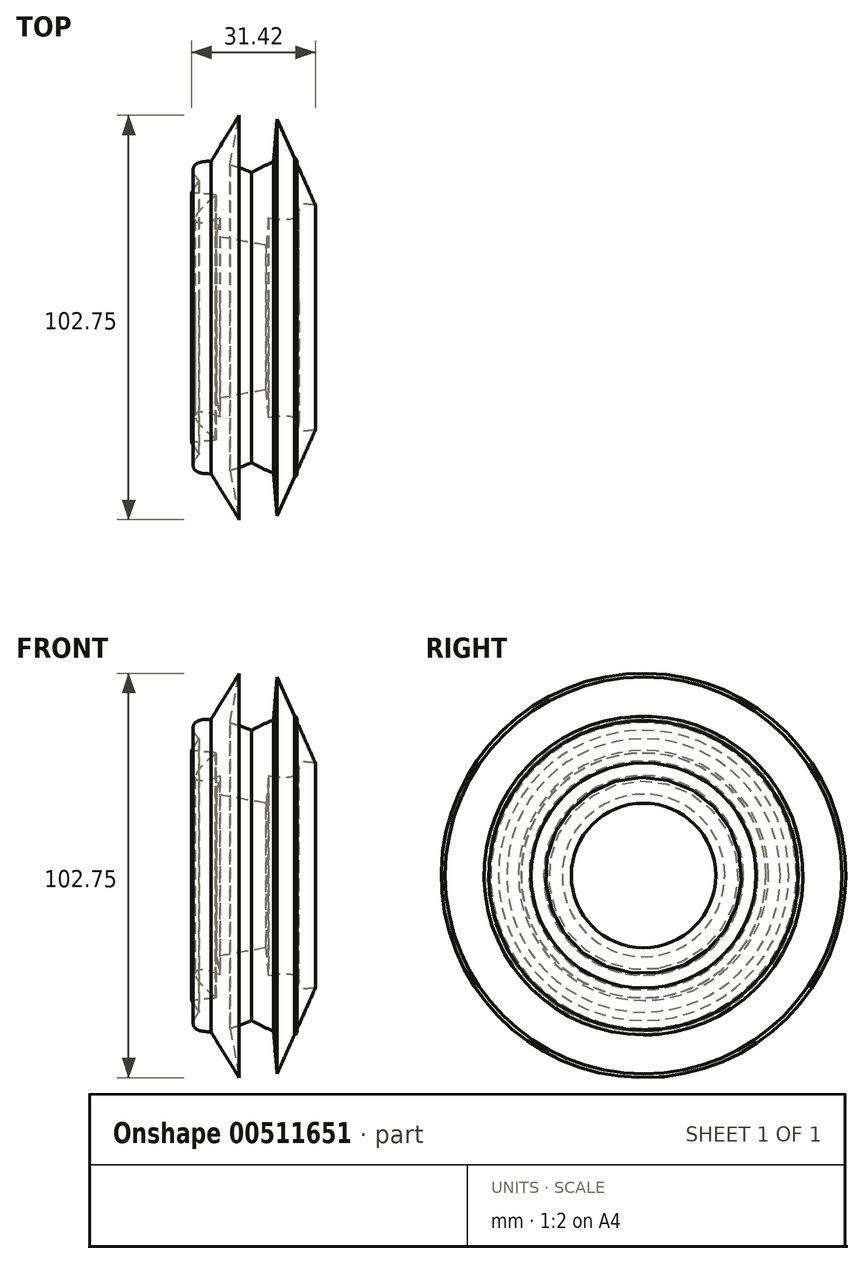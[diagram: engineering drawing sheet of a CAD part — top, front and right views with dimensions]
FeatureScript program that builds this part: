
annotation { "Feature Type Name" : "Feature", "Feature Type Description" : "" }
export const myFeature = defineFeature(function(context is Context, id is Id, definition is map)
    precondition{}
    {
        {
            var Q0;
            Q0=qCreatedBy(makeId("Front.planeOp"),FACE);
            var sketch = newSketch(context, id + "F0", { "sketchPlane" : qUnion([Q0])});
            skEllipse(sketch, "E0", {"center": v(0, -41.42) * mm, "majorRadius": 14.6 * mm, "minorRadius": 4.76 * mm, "majorAxis": v(0.9, 0.41)});
            skEllipse(sketch, "E1", {"center": v(0, -41.42) * mm, "majorRadius": 15.03 * mm, "minorRadius": 3.32 * mm, "majorAxis": v(-0.85, 0.52)});
            skLineSegment(sketch, "E2", {"start": v(-13.82, -40.88) * mm, "end": v(-1.74, -60.59) * mm});
            skPoint(sketch, "E2.endSnap0", {"position": v(-1.74, -44.24) * mm});
            skLineSegment(sketch, "E3", {"start": v(-1.74, -60.59) * mm, "end": v(-7.49, -29.63) * mm});
            skLineSegment(sketch, "E4", {"start": v(-7.49, -29.63) * mm, "end": v(5.09, -27.3) * mm});
            skLineSegment(sketch, "E5", {"start": v(5.09, -27.3) * mm, "end": v(7.92, -59.6) * mm});
            skLineSegment(sketch, "E6", {"start": v(7.92, -59.6) * mm, "end": v(17.6, -37.67) * mm});
            skLineSegment(sketch, "E7", {"start": v(17.6, -37.67) * mm, "end": v(-13.82, -40.88) * mm});
            skSolve(sketch);
        }
        {
            var Q0;
            Q0=qCreatedBy(makeId("Right.planeOp"),FACE);
            var sketch = newSketch(context, id + "F1", { "sketchPlane" : qUnion([Q0])});
            skCircle(sketch, "E8", {"center": v(-3.89, -9.36) * mm, "radius": 19.61 * mm});
            skPoint(sketch, "E8.first.point", {"position": v(15.7, -8.2) * mm});
            skPoint(sketch, "E8.second.point", {"position": v(-14.22, -26.03) * mm});
            skPoint(sketch, "E8.third.point", {"position": v(0, 9.87) * mm});
            skSolve(sketch);
        }
        {
            var Q0;
            Q0 = qSketchRegion(id + "F0", true);
            var Q1;
            Q1 = qConstructionFilter(qBodyType(qCreatedBy(id + "F1" ,EDGE), BodyType.WIRE), ConstructionObject.NO);
            sweep(context, id + "F2", {"profiles" : qUnion([Q0]), "path" : qUnion([Q1])});
        }
    });
